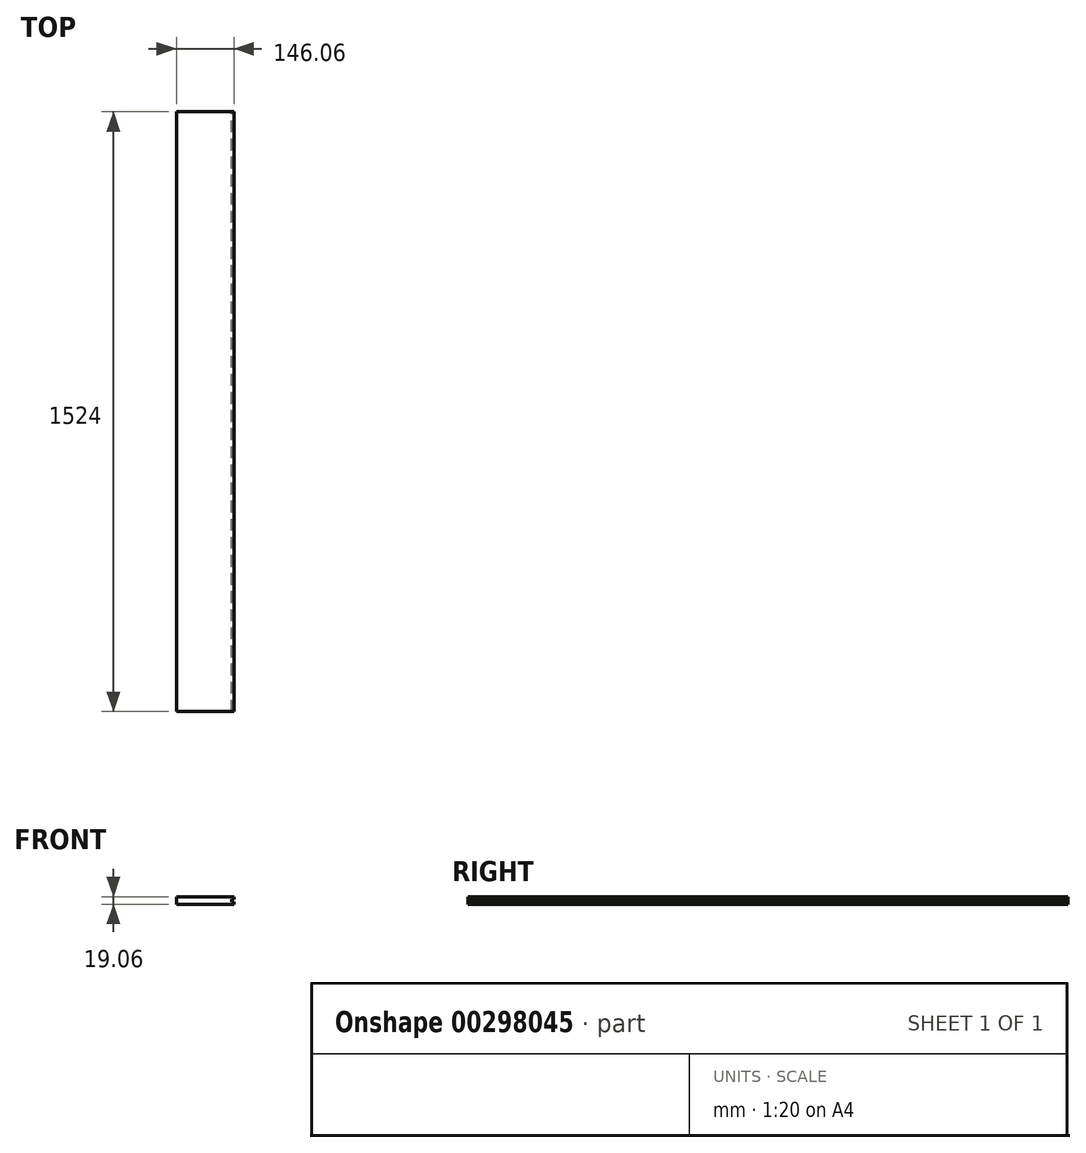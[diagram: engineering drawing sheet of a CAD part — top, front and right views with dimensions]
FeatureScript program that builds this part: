
annotation { "Feature Type Name" : "Feature", "Feature Type Description" : "" }
export const myFeature = defineFeature(function(context is Context, id is Id, definition is map)
    precondition{}
    {
        {
            var Q0;
            Q0=qCreatedBy(makeId("Front.planeOp"),FACE);
            var sketch = newSketch(context, id + "F0", { "sketchPlane" : qUnion([Q0])});
            skLineSegment(sketch, "E0.bottom", {"start": v(-73.03, -9.53) * mm, "end": v(73.03, -9.53) * mm});
            skLineSegment(sketch, "E0.top", {"start": v(-73.03, 9.52) * mm, "end": v(73.03, 9.52) * mm});
            skLineSegment(sketch, "E0.left", {"start": v(-73.03, -9.53) * mm, "end": v(-73.03, 9.53) * mm});
            skLineSegment(sketch, "E0.right", {"start": v(73.03, -9.53) * mm, "end": v(73.03, 9.53) * mm});
            skPoint(sketch, "E0.middle", {"position": v(0, 0) * mm});
            skLineSegment(sketch, "E1.bottom", {"start": v(-73.03, 3.18) * mm, "end": v(-66.68, 3.18) * mm});
            skLineSegment(sketch, "E1.top", {"start": v(-73.03, -3.17) * mm, "end": v(-66.68, -3.17) * mm});
            skLineSegment(sketch, "E1.left", {"start": v(-73.03, 3.18) * mm, "end": v(-73.03, -3.17) * mm});
            skLineSegment(sketch, "E1.right", {"start": v(-66.68, 3.18) * mm, "end": v(-66.68, -3.17) * mm});
            skPoint(sketch, "E1.middle", {"position": v(-69.85, 0) * mm});
            skLineSegment(sketch, "E2.bottom", {"start": v(73.03, 3.18) * mm, "end": v(66.67, 3.18) * mm});
            skLineSegment(sketch, "E2.top", {"start": v(73.02, -3.17) * mm, "end": v(66.67, -3.17) * mm});
            skLineSegment(sketch, "E2.left", {"start": v(73.03, 3.18) * mm, "end": v(73.03, -3.17) * mm});
            skLineSegment(sketch, "E2.right", {"start": v(66.67, 3.18) * mm, "end": v(66.67, -3.17) * mm});
            skPoint(sketch, "E2.middle", {"position": v(69.85, 0) * mm});
            skSolve(sketch);
        }
        {
            var Q0;
            {var subQ6=sQuery(id+"F0.wireOp",EDGE,"E0.bottom");Q0=makeQuery(id+"F0.imprint","IMPRINT",FACE,{"disambiguationData":[TD([[makeQuery(id+"F0.imprint","IMPRINT",EDGE,{"derivedFrom":subQ6}),1.0]])]});}
            var Q1;
            Q1=makeQuery(id+"F0.imprint","IMPRINT",FACE,{"disambiguationData":[TD([[makeQuery(id+"F0.imprint","IMPRINT",EDGE,{"derivedFrom":sQuery(id+"F0.wireOp",EDGE,"E1.bottom")}),-1.0]])]});
            extrude(context, id + "F1", {"entities" : qUnion([Q0, Q1]), "endBound" : BoundingType.SYMMETRIC, "depth" : 1524 * mm});
        }
    });
